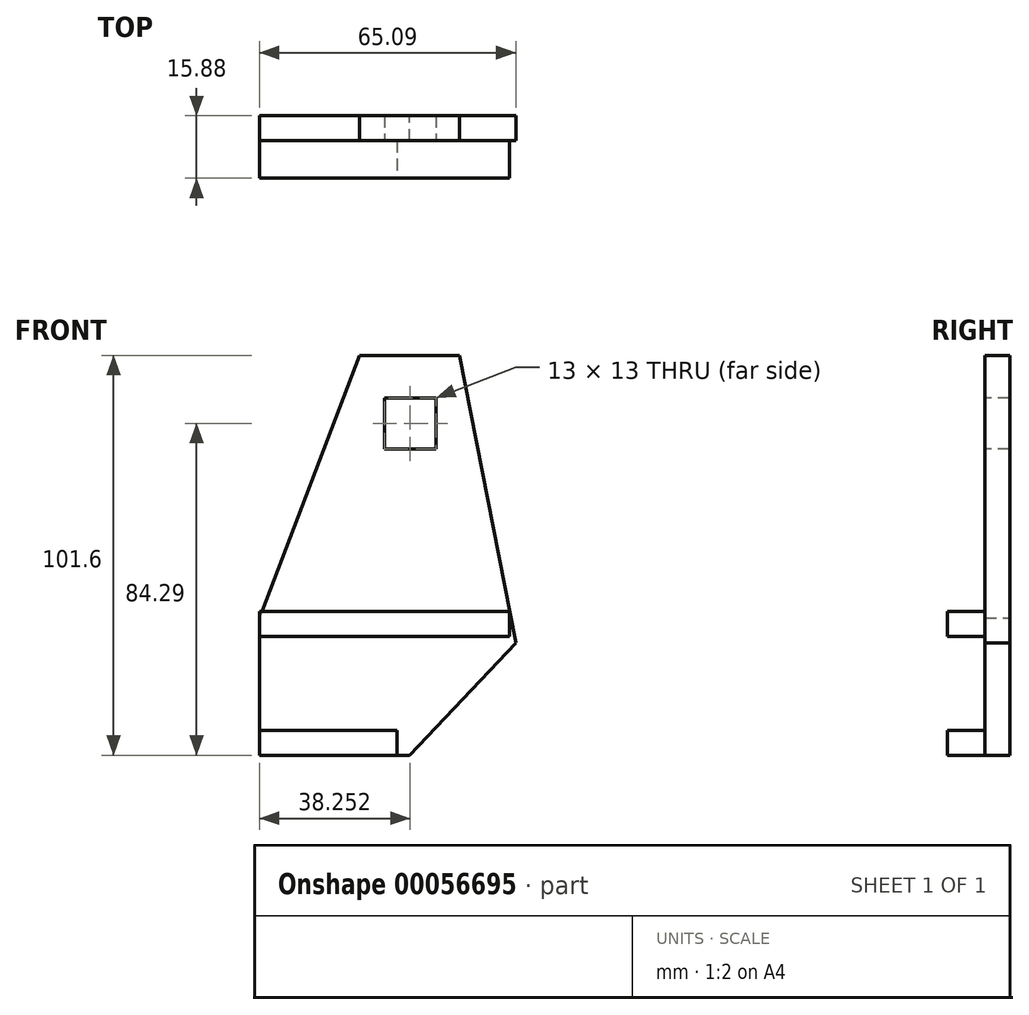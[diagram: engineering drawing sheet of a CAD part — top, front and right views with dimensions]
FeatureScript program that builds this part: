
annotation { "Feature Type Name" : "Feature", "Feature Type Description" : "" }
export const myFeature = defineFeature(function(context is Context, id is Id, definition is map)
    precondition{}
    {
        {
            var Q0;
            Q0=qCreatedBy(makeId("Front.planeOp"),FACE);
            var sketch = newSketch(context, id + "F0", { "sketchPlane" : qUnion([Q0])});
            skLineSegment(sketch, "E0", {"start": v(0, 0) * mm, "end": v(0, 34.92) * mm});
            skLineSegment(sketch, "E1", {"start": v(0, 34.92) * mm, "end": v(25.4, 101.6) * mm});
            skLineSegment(sketch, "E2", {"start": v(25.4, 101.6) * mm, "end": v(50.8, 101.6) * mm});
            skLineSegment(sketch, "E3", {"start": v(50.8, 101.6) * mm, "end": v(65.09, 28.58) * mm});
            skLineSegment(sketch, "E4", {"start": v(65.09, 28.58) * mm, "end": v(38.1, 0) * mm});
            skLineSegment(sketch, "E5", {"start": v(38.1, 0) * mm, "end": v(0, 0) * mm});
            skSolve(sketch);
        }
        {
            var Q0;
            Q0=makeQuery(id+"F0.imprint","IMPRINT",FACE,{"disambiguationData":[TD([[makeQuery(id+"F0.imprint","IMPRINT",EDGE,{"derivedFrom":sQuery(id+"F0.wireOp",EDGE,"E0")}),-1.0]])]});
            extrude(context, id + "F1", {"entities" : qUnion([Q0]), "depth" : 6.35 * mm});
        }
        {
            var Q0;
            Q0=makeQuery(id+"F1.opExtrude","CAP_FACE",FACE,{"disambiguationData":[OSD([sQuery(id+"F0.wireOp",EDGE,"E0"),sQuery(id+"F0.wireOp",EDGE,"E1"),sQuery(id+"F0.wireOp",EDGE,"E2"),sQuery(id+"F0.wireOp",EDGE,"E3"),sQuery(id+"F0.wireOp",EDGE,"E4"),sQuery(id+"F0.wireOp",EDGE,"E5")])],"isStart":false});
            var sketch = newSketch(context, id + "F2", { "sketchPlane" : qUnion([Q0])});
            skLineSegment(sketch, "E6.bottom", {"start": v(31.75, 90.8) * mm, "end": v(44.75, 90.8) * mm});
            skLineSegment(sketch, "E6.top", {"start": v(31.75, 77.79) * mm, "end": v(44.75, 77.79) * mm});
            skLineSegment(sketch, "E6.left", {"start": v(31.75, 90.8) * mm, "end": v(31.75, 77.79) * mm});
            skLineSegment(sketch, "E6.right", {"start": v(44.75, 90.8) * mm, "end": v(44.75, 77.79) * mm});
            skSolve(sketch);
        }
        {
            var Q0;
            Q0 = qSketchRegion(id + "F2", true);
            extrude(context, id + "F3", {"entities" : qUnion([Q0]), "operationType" : NewBodyOperationType.REMOVE, "oppositeDirection" : true, "depth" : 25.4 * mm});
        }
        {
            var Q0;
            Q0=makeQuery(id+"F1.opExtrude","SWEPT_FACE",FACE,{"disambiguationData":[OSD([sQuery(id+"F0.wireOp",EDGE,"E0")])]});
            var sketch = newSketch(context, id + "F4", { "sketchPlane" : qUnion([Q0])});
            skLineSegment(sketch, "E7.bottom", {"start": v(6.35, 0) * mm, "end": v(15.88, 0) * mm});
            skLineSegment(sketch, "E7.top", {"start": v(6.35, 6.35) * mm, "end": v(15.88, 6.35) * mm});
            skLineSegment(sketch, "E7.left", {"start": v(6.35, 0) * mm, "end": v(6.35, 6.35) * mm});
            skLineSegment(sketch, "E7.right", {"start": v(15.88, 0) * mm, "end": v(15.88, 6.35) * mm});
            skSolve(sketch);
        }
        {
            var Q0;
            Q0 = qSketchRegion(id + "F4", true);
            extrude(context, id + "F5", {"entities" : qUnion([Q0]), "oppositeDirection" : true, "depth" : 34.92 * mm});
        }
        {
            var Q0;
            Q0=makeQuery(id+"F1.opExtrude","SWEPT_FACE",FACE,{"disambiguationData":[OSD([sQuery(id+"F0.wireOp",EDGE,"E0")])]});
            var sketch = newSketch(context, id + "F6", { "sketchPlane" : qUnion([Q0])});
            skLineSegment(sketch, "E8.bottom", {"start": v(6.35, 36.51) * mm, "end": v(15.87, 36.51) * mm});
            skLineSegment(sketch, "E8.top", {"start": v(6.35, 30.16) * mm, "end": v(15.87, 30.16) * mm});
            skLineSegment(sketch, "E8.left", {"start": v(6.35, 36.51) * mm, "end": v(6.35, 30.16) * mm});
            skLineSegment(sketch, "E8.right", {"start": v(15.88, 36.51) * mm, "end": v(15.88, 30.16) * mm});
            skSolve(sketch);
        }
        {
            var Q0;
            Q0 = qSketchRegion(id + "F6", true);
            extrude(context, id + "F7", {"entities" : qUnion([Q0]), "oppositeDirection" : true, "depth" : 63.5 * mm});
        }
    });
